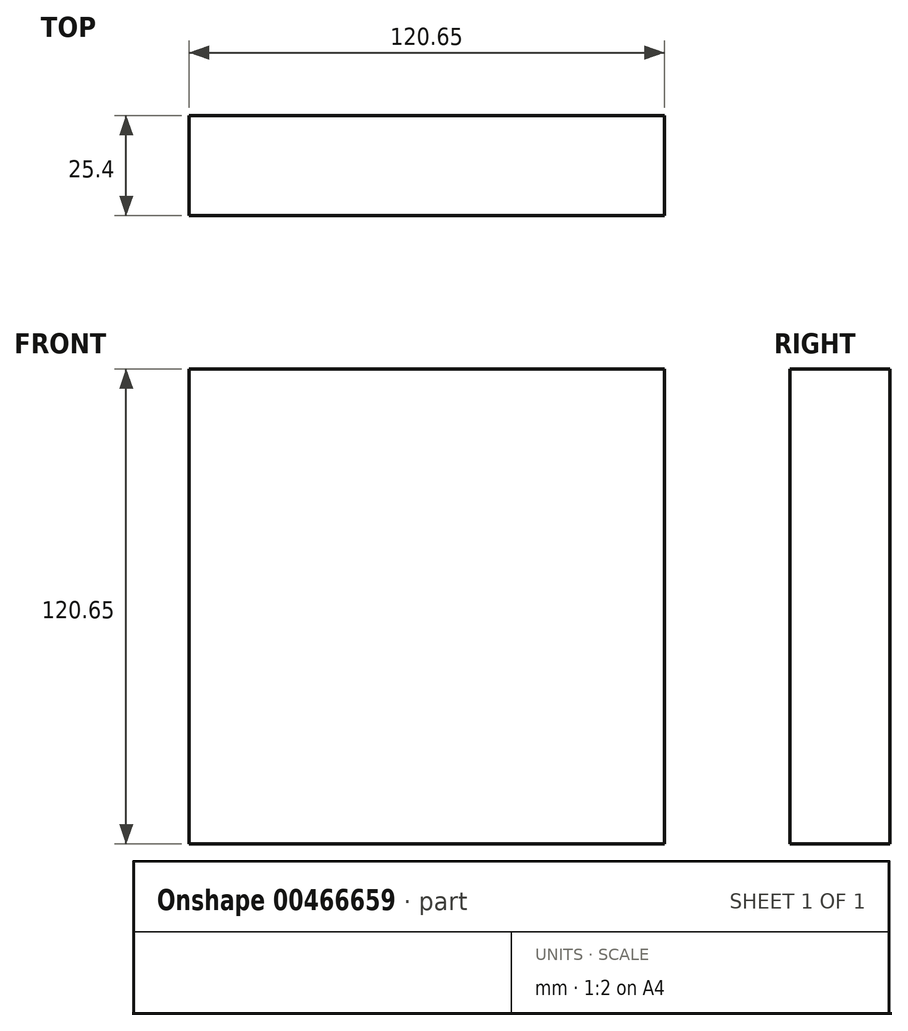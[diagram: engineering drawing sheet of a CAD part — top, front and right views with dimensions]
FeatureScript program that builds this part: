
annotation { "Feature Type Name" : "Feature", "Feature Type Description" : "" }
export const myFeature = defineFeature(function(context is Context, id is Id, definition is map)
    precondition{}
    {
        {
            var Q0;
            Q0=qCreatedBy(makeId("Front.planeOp"),FACE);
            var sketch = newSketch(context, id + "F0", { "sketchPlane" : qUnion([Q0])});
            skLineSegment(sketch, "E0.bottom", {"start": v(0, 0) * mm, "end": v(-120.65, 0) * mm});
            skLineSegment(sketch, "E0.top", {"start": v(0, 120.65) * mm, "end": v(-120.65, 120.65) * mm});
            skLineSegment(sketch, "E0.left", {"start": v(0, 0) * mm, "end": v(0, 120.65) * mm});
            skLineSegment(sketch, "E0.right", {"start": v(-120.65, 0) * mm, "end": v(-120.65, 120.65) * mm});
            skSolve(sketch);
        }
        {
            var Q0;
            Q0 = qSketchRegion(id + "F0", true);
            extrude(context, id + "F1", {"entities" : qUnion([Q0]), "depth" : 25.4 * mm});
        }
    });
